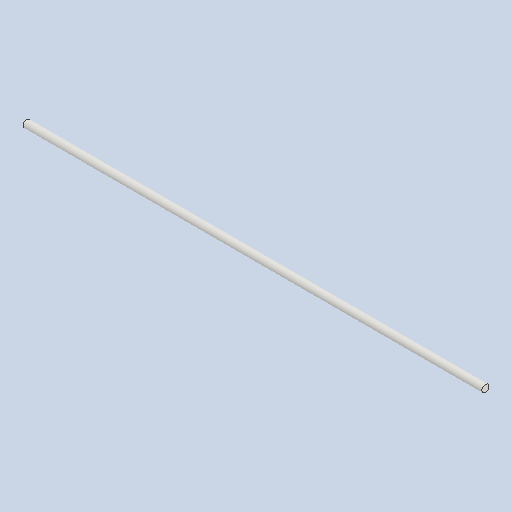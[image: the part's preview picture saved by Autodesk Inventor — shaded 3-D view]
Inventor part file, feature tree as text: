
AUTODESK INVENTOR PART (.ipt)
format: ipt  version: 2023 (Build 270158000, 158)  size: 73,728 bytes
history: native  units: mm
features: other x3, revolve x1
ambient origin geometry x6: Origin, XZ Plane, XY Plane, X Axis, Y Axis, Z Axis
bodies: Solid1 (feature_tree)
feature tree (4):
  revolve  "Revolution1"  [1 undecoded]
  other  "Start Plane"
  other  "Origin point"
  other  "Main Sketch"
note: 1 required parameter value undecoded (feature->parameter linkage not recoverable at this tier; creation-order binding heuristic only, values carry confidence <= 0.55)
